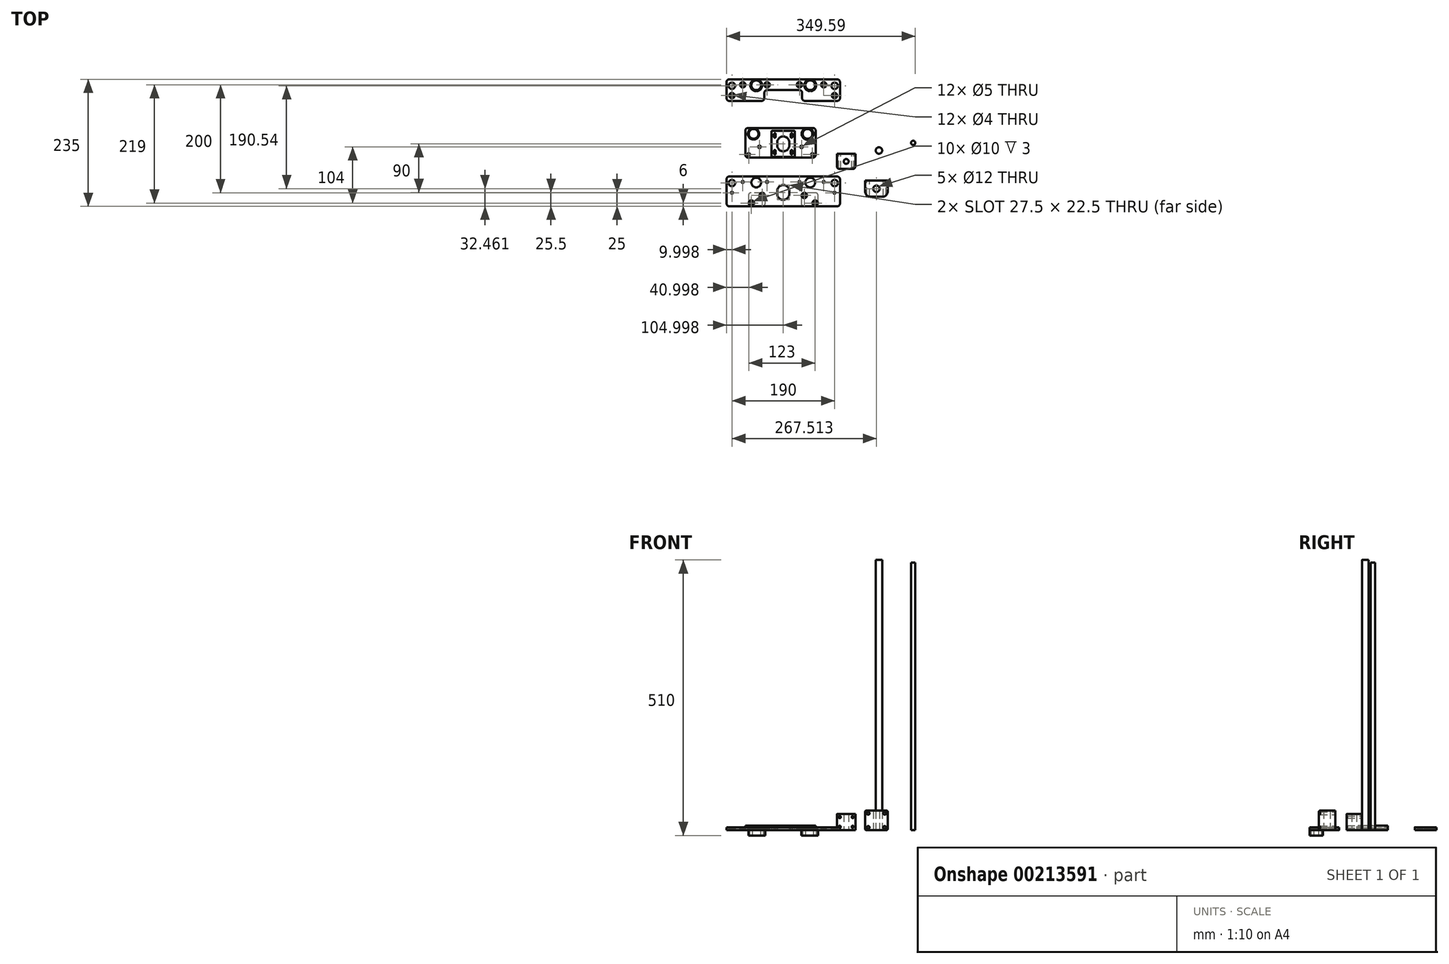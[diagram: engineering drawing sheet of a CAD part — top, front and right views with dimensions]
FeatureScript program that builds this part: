
annotation { "Feature Type Name" : "Feature", "Feature Type Description" : "" }
export const myFeature = defineFeature(function(context is Context, id is Id, definition is map)
    precondition{}
    {
        {
            var Q0;
            Q0=qCreatedBy(makeId("Top.planeOp"),FACE);
            var sketch = newSketch(context, id + "F0", { "sketchPlane" : qUnion([Q0])});
            skCircle(sketch, "E0", {"center": v(45.06, 37.07) * mm, "radius": 6 * mm});
            skSolve(sketch);
        }
        {
            var Q0;
            Q0=makeQuery(id+"F0.imprint","IMPRINT",FACE,{"disambiguationData":[TD([[makeQuery(id+"F0.imprint","IMPRINT",EDGE,{"derivedFrom":sQuery(id+"F0.wireOp",EDGE,"E0")}),1.0]])]});
            extrude(context, id + "F1", {"entities" : qUnion([Q0]), "depth" : 500 * mm});
        }
        {
            var Q0;
            Q0=qCreatedBy(makeId("Top.planeOp"),FACE);
            var sketch = newSketch(context, id + "F2", { "sketchPlane" : qUnion([Q0])});
            skLineSegment(sketch, "E1", {"start": v(-202.1, 78.9) * mm, "end": v(-202.1, 23.9) * mm});
            skLineSegment(sketch, "E2", {"start": v(-202.1, 23.9) * mm, "end": v(-72.1, 23.9) * mm});
            skLineSegment(sketch, "E3", {"start": v(-72.1, 23.9) * mm, "end": v(-72.1, 78.9) * mm});
            skLineSegment(sketch, "E4", {"start": v(-72.1, 78.9) * mm, "end": v(-202.1, 78.9) * mm});
            skCircle(sketch, "E5", {"center": v(-187.1, 67.9) * mm, "radius": 9 * mm});
            skCircle(sketch, "E6", {"center": v(-87.1, 67.9) * mm, "radius": 9 * mm});
            skLineSegment(sketch, "E7", {"start": v(-153.6, 25.4) * mm, "end": v(-153.6, 73.4) * mm});
            skLineSegment(sketch, "E8", {"start": v(-153.6, 73.4) * mm, "end": v(-110.6, 73.4) * mm});
            skLineSegment(sketch, "E9", {"start": v(-110.6, 73.4) * mm, "end": v(-110.6, 25.4) * mm});
            skLineSegment(sketch, "E10", {"start": v(-110.6, 25.4) * mm, "end": v(-153.6, 25.4) * mm});
            skLineSegment(sketch, "E11", {"start": v(-132.1, 73.4) * mm, "end": v(-132.1, 25.4) * mm, "construction": true});
            skLineSegment(sketch, "E12", {"start": v(-132.1, 49.4) * mm, "end": v(-143.35, 49.4) * mm, "construction": true});
            skLineSegment(sketch, "E13", {"start": v(-132.1, 49.4) * mm, "end": v(-120.85, 49.4) * mm, "construction": true});
            skLineSegment(sketch, "E14", {"start": v(-143.35, 51.9) * mm, "end": v(-143.35, 46.9) * mm});
            skLineSegment(sketch, "E15", {"start": v(-120.85, 51.9) * mm, "end": v(-120.85, 46.9) * mm});
            skArc(sketch, "E16", {"start": v(-120.85, 51.9) * mm, "mid": v(-132.1, 63.15) * mm, "end": v(-143.35, 51.9) * mm});
            skArc(sketch, "E17", {"start": v(-143.35, 46.9) * mm, "mid": v(-132.1, 35.65) * mm, "end": v(-120.85, 46.9) * mm});
            skLineSegment(sketch, "E18", {"start": v(-149.15, 36.4) * mm, "end": v(-149.15, 31.4) * mm});
            skLineSegment(sketch, "E19", {"start": v(-146.05, 36.4) * mm, "end": v(-146.05, 31.4) * mm});
            skArc(sketch, "E20", {"start": v(-146.05, 36.4) * mm, "mid": v(-147.6, 37.95) * mm, "end": v(-149.15, 36.4) * mm});
            skArc(sketch, "E21", {"start": v(-149.15, 31.4) * mm, "mid": v(-147.6, 29.85) * mm, "end": v(-146.05, 31.4) * mm});
            skLineSegment(sketch, "E22", {"start": v(-149.15, 33.9) * mm, "end": v(-146.05, 33.9) * mm, "construction": true});
            skLineSegment(sketch, "E23", {"start": v(-118.15, 36.4) * mm, "end": v(-118.15, 31.4) * mm});
            skLineSegment(sketch, "E24", {"start": v(-115.05, 36.4) * mm, "end": v(-115.05, 31.4) * mm});
            skArc(sketch, "E25", {"start": v(-115.05, 36.4) * mm, "mid": v(-116.6, 37.95) * mm, "end": v(-118.15, 36.4) * mm});
            skArc(sketch, "E26", {"start": v(-118.15, 31.4) * mm, "mid": v(-116.6, 29.85) * mm, "end": v(-115.05, 31.4) * mm});
            skLineSegment(sketch, "E27", {"start": v(-118.15, 33.9) * mm, "end": v(-115.05, 33.9) * mm, "construction": true});
            skLineSegment(sketch, "E28", {"start": v(-149.15, 67.4) * mm, "end": v(-149.15, 62.4) * mm});
            skLineSegment(sketch, "E29", {"start": v(-146.05, 67.4) * mm, "end": v(-146.05, 62.4) * mm});
            skArc(sketch, "E30", {"start": v(-146.05, 67.4) * mm, "mid": v(-147.6, 68.95) * mm, "end": v(-149.15, 67.4) * mm});
            skArc(sketch, "E31", {"start": v(-149.15, 62.4) * mm, "mid": v(-147.6, 60.85) * mm, "end": v(-146.05, 62.4) * mm});
            skLineSegment(sketch, "E32", {"start": v(-149.15, 64.9) * mm, "end": v(-146.05, 64.9) * mm, "construction": true});
            skLineSegment(sketch, "E33", {"start": v(-118.15, 67.4) * mm, "end": v(-118.15, 62.4) * mm});
            skLineSegment(sketch, "E34", {"start": v(-115.05, 67.4) * mm, "end": v(-115.05, 62.4) * mm});
            skArc(sketch, "E35", {"start": v(-115.05, 67.4) * mm, "mid": v(-116.6, 68.95) * mm, "end": v(-118.15, 67.4) * mm});
            skArc(sketch, "E36", {"start": v(-118.15, 62.4) * mm, "mid": v(-116.6, 60.85) * mm, "end": v(-115.05, 62.4) * mm});
            skLineSegment(sketch, "E37", {"start": v(-118.15, 64.9) * mm, "end": v(-115.05, 64.9) * mm, "construction": true});
            skCircle(sketch, "E38", {"center": v(-78.1, 29.9) * mm, "radius": 2.5 * mm});
            skCircle(sketch, "E39", {"center": v(-196.1, 29.9) * mm, "radius": 2.5 * mm});
            skCircle(sketch, "E40", {"center": v(-176.1, 43.9) * mm, "radius": 2.5 * mm});
            skCircle(sketch, "E41", {"center": v(-98.1, 43.9) * mm, "radius": 2.5 * mm});
            skSolve(sketch);
        }
        {
            var Q0;
            Q0=makeQuery(id+"F2.imprint","IMPRINT",FACE,{"disambiguationData":[TD([[makeQuery(id+"F2.imprint","IMPRINT",EDGE,{"derivedFrom":sQuery(id+"F2.wireOp",EDGE,"E1")}),1.0]])]});
            extrude(context, id + "F3", {"entities" : qUnion([Q0]), "depth" : 8 * mm});
        }
        {
            var Q0;
            Q0=makeQuery(id+"F2.imprint","IMPRINT",FACE,{"disambiguationData":[TD([[makeQuery(id+"F2.imprint","IMPRINT",EDGE,{"derivedFrom":sQuery(id+"F2.wireOp",EDGE,"E7")}),-1.0]])]});
            extrude(context, id + "F4", {"entities" : qUnion([Q0]), "operationType" : NewBodyOperationType.ADD, "depth" : 4 * mm});
        }
        {
            var Q0;
            Q0=makeQuery(id+"F3.opExtrude","SWEPT_EDGE",EDGE,{"disambiguationData":[OSD([sQuery(id+"F2.wireOp",EDGE,"E7"),sQuery(id+"F2.wireOp",EDGE,"E8")])]});
            var Q1;
            Q1=makeQuery(id+"F3.opExtrude","SWEPT_EDGE",EDGE,{"disambiguationData":[OSD([sQuery(id+"F2.wireOp",EDGE,"E8"),sQuery(id+"F2.wireOp",EDGE,"E9")])]});
            var Q2;
            Q2=makeQuery(id+"F3.opExtrude","SWEPT_EDGE",EDGE,{"disambiguationData":[OSD([sQuery(id+"F2.wireOp",EDGE,"E9"),sQuery(id+"F2.wireOp",EDGE,"E10")])]});
            var Q3;
            Q3=makeQuery(id+"F3.opExtrude","SWEPT_EDGE",EDGE,{"disambiguationData":[OSD([sQuery(id+"F2.wireOp",EDGE,"E7"),sQuery(id+"F2.wireOp",EDGE,"E10")])]});
            fillet(context, id + "F5", {"entities" : qUnion([Q0, Q1, Q2, Q3]), "radius" : 1 * mm, "tangentPropagation" : true, "allowEdgeOverflow" : false});
        }
        {
            var Q0;
            Q0=makeQuery(id+"F3.opExtrude","CAP_FACE",FACE,{"disambiguationData":[OSD([sQuery(id+"F2.wireOp",EDGE,"E1"),sQuery(id+"F2.wireOp",EDGE,"E2"),sQuery(id+"F2.wireOp",EDGE,"E3"),sQuery(id+"F2.wireOp",EDGE,"E4"),sQuery(id+"F2.wireOp",EDGE,"E5"),sQuery(id+"F2.wireOp",EDGE,"E6"),sQuery(id+"F2.wireOp",EDGE,"E7"),sQuery(id+"F2.wireOp",EDGE,"E8"),sQuery(id+"F2.wireOp",EDGE,"E9"),sQuery(id+"F2.wireOp",EDGE,"E10")])],"isStart":false});
            var sketch = newSketch(context, id + "F6", { "sketchPlane" : qUnion([Q0])});
            skCircle(sketch, "E42", {"center": v(-187.1, 67.9) * mm, "radius": 10.5 * mm});
            skLineSegment(sketch, "E43", {"start": v(-194.1, 75.73) * mm, "end": v(-194.1, 78.9) * mm});
            skLineSegment(sketch, "E44", {"start": v(-180.1, 75.73) * mm, "end": v(-180.1, 78.9) * mm});
            skCircle(sketch, "E45", {"center": v(-87.1, 67.9) * mm, "radius": 11 * mm});
            skLineSegment(sketch, "E46", {"start": v(-94.1, 76.39) * mm, "end": v(-94.1, 78.9) * mm});
            skLineSegment(sketch, "E47", {"start": v(-80.1, 76.39) * mm, "end": v(-80.1, 78.9) * mm});
            skSolve(sketch);
        }
        {
            var Q0;
            Q0=makeQuery(id+"F6.imprint","IMPRINT",FACE,{"disambiguationData":[TD([[makeQuery(id+"F6.imprint","IMPRINT",EDGE,{"derivedFrom":sQuery(id+"F6.wireOp",EDGE,"GBhv8pRL-lCPt-Fi0s-pCJl-KyG8ppzGTcWA")}),1.0]])]});
            var Q1;
            Q1=makeQuery(id+"F6.imprint","IMPRINT",FACE,{"disambiguationData":[TD([[makeQuery(id+"F6.imprint","IMPRINT",EDGE,{"derivedFrom":sQuery(id+"F6.wireOp",EDGE,"E42")}),1.0]])]});
            var Q2;
            {var subQ0=sQuery(id+"F6.wireOp",EDGE,"E43");Q2=makeQuery(id+"F6.imprint","IMPRINT",FACE,{"disambiguationData":[TD([[makeQuery(id+"F6.imprint","IMPRINT",EDGE,{"derivedFrom":subQ0}),-1.0]])]});}
            var Q3;
            {var subQ0=sQuery(id+"F6.wireOp",EDGE,"E44");Q3=makeQuery(id+"F6.imprint","IMPRINT",FACE,{"disambiguationData":[TD([[makeQuery(id+"F6.imprint","IMPRINT",EDGE,{"derivedFrom":subQ0}),1.0]])]});}
            var Q4;
            Q4=makeQuery(id+"F6.imprint","IMPRINT",FACE,{"disambiguationData":[TD([[makeQuery(id+"F6.imprint","IMPRINT",EDGE,{"derivedFrom":makeQuery(id+"F3.opExtrude","CAP_EDGE",EDGE,{"disambiguationData":[OSD([sQuery(id+"F2.wireOp",EDGE,"E6")])],"isStart":false})}),-1.0]])]});
            var Q5;
            {var subQ0=sQuery(id+"F6.wireOp",EDGE,"E46");Q5=makeQuery(id+"F6.imprint","IMPRINT",FACE,{"disambiguationData":[TD([[makeQuery(id+"F6.imprint","IMPRINT",EDGE,{"derivedFrom":subQ0}),-1.0]])]});}
            var Q6;
            {var subQ0=sQuery(id+"F6.wireOp",EDGE,"E47");Q6=makeQuery(id+"F6.imprint","IMPRINT",FACE,{"disambiguationData":[TD([[makeQuery(id+"F6.imprint","IMPRINT",EDGE,{"derivedFrom":subQ0}),1.0]])]});}
            extrude(context, id + "F7", {"entities" : qUnion([Q0, Q1, Q2, Q3, Q4, Q5, Q6]), "operationType" : NewBodyOperationType.REMOVE, "oppositeDirection" : true, "depth" : 5 * mm});
        }
        {
            var Q0;
            Q0=makeQuery(id+"F3.opExtrude","SWEPT_EDGE",EDGE,{"disambiguationData":[OSD([sQuery(id+"F2.wireOp",EDGE,"E1"),sQuery(id+"F2.wireOp",EDGE,"E4")])]});
            var Q1;
            Q1=makeQuery(id+"F3.opExtrude","SWEPT_EDGE",EDGE,{"disambiguationData":[OSD([sQuery(id+"F2.wireOp",EDGE,"E1"),sQuery(id+"F2.wireOp",EDGE,"E2")])]});
            var Q2;
            Q2=makeQuery(id+"F3.opExtrude","SWEPT_EDGE",EDGE,{"disambiguationData":[OSD([sQuery(id+"F2.wireOp",EDGE,"E2"),sQuery(id+"F2.wireOp",EDGE,"E3")])]});
            var Q3;
            Q3=makeQuery(id+"F3.opExtrude","SWEPT_EDGE",EDGE,{"disambiguationData":[OSD([sQuery(id+"F2.wireOp",EDGE,"E3"),sQuery(id+"F2.wireOp",EDGE,"E4")])]});
            fillet(context, id + "F8", {"entities" : qUnion([Q0, Q1, Q2, Q3]), "radius" : 5 * mm, "tangentPropagation" : true, "allowEdgeOverflow" : false});
        }
        {
            var Q0;
            Q0=qCreatedBy(makeId("Top.planeOp"),FACE);
            var sketch = newSketch(context, id + "F9", { "sketchPlane" : qUnion([Q0])});
            skLineSegment(sketch, "E48", {"start": v(-237.1, -11.1) * mm, "end": v(-237.1, -66.1) * mm});
            skLineSegment(sketch, "E49", {"start": v(-237.1, -66.1) * mm, "end": v(-27.1, -66.1) * mm});
            skLineSegment(sketch, "E50", {"start": v(-27.1, -66.1) * mm, "end": v(-27.1, -11.1) * mm});
            skLineSegment(sketch, "E51", {"start": v(-27.1, -11.1) * mm, "end": v(-237.1, -11.1) * mm});
            skLineSegment(sketch, "E52", {"start": v(-132.1, -40.6) * mm, "end": v(-143.35, -40.6) * mm, "construction": true});
            skLineSegment(sketch, "E53", {"start": v(-132.1, -40.6) * mm, "end": v(-120.85, -40.6) * mm, "construction": true});
            skLineSegment(sketch, "E54", {"start": v(-143.35, -38.1) * mm, "end": v(-143.35, -43.1) * mm});
            skLineSegment(sketch, "E55", {"start": v(-120.85, -38.1) * mm, "end": v(-120.85, -43.1) * mm});
            skArc(sketch, "E56", {"start": v(-120.85, -38.1) * mm, "mid": v(-132.1, -26.85) * mm, "end": v(-143.35, -38.1) * mm});
            skArc(sketch, "E57", {"start": v(-143.35, -43.1) * mm, "mid": v(-132.1, -54.35) * mm, "end": v(-120.85, -43.1) * mm});
            skCircle(sketch, "E58", {"center": v(-73.1, -60.1) * mm, "radius": 2.5 * mm});
            skCircle(sketch, "E59", {"center": v(-191.1, -60.1) * mm, "radius": 2.5 * mm});
            skCircle(sketch, "E60", {"center": v(-171.1, -46.1) * mm, "radius": 2.5 * mm});
            skCircle(sketch, "E61", {"center": v(-93.1, -46.1) * mm, "radius": 2.5 * mm});
            skCircle(sketch, "E62", {"center": v(-227.1, -23.1) * mm, "radius": 6 * mm});
            skCircle(sketch, "E63", {"center": v(-37.1, -23.1) * mm, "radius": 6 * mm});
            skCircle(sketch, "E64", {"center": v(-207.1, -21.1) * mm, "radius": 2 * mm});
            skCircle(sketch, "E65", {"center": v(-57.1, -21.1) * mm, "radius": 2 * mm});
            skCircle(sketch, "E66", {"center": v(-102.1, -21.1) * mm, "radius": 2 * mm});
            skCircle(sketch, "E67", {"center": v(-162.1, -21.1) * mm, "radius": 2 * mm});
            skCircle(sketch, "E68", {"center": v(-227.1, -41.1) * mm, "radius": 2 * mm});
            skCircle(sketch, "E69", {"center": v(-37.1, -41.1) * mm, "radius": 2 * mm});
            skCircle(sketch, "E70", {"center": v(-82.1, -22.1) * mm, "radius": 9 * mm});
            skCircle(sketch, "E71", {"center": v(-182.1, -22.1) * mm, "radius": 9 * mm});
            skSolve(sketch);
        }
        {
            var Q0;
            Q0=makeQuery(id+"F9.imprint","IMPRINT",FACE,{"disambiguationData":[TD([[makeQuery(id+"F9.imprint","IMPRINT",EDGE,{"derivedFrom":sQuery(id+"F9.wireOp",EDGE,"E48")}),1.0]])]});
            extrude(context, id + "F10", {"entities" : qUnion([Q0]), "depth" : 5 * mm});
        }
        {
            var Q0;
            Q0=makeQuery(id+"F10.opExtrude","CAP_FACE",FACE,{"disambiguationData":[OSD([sQuery(id+"F9.wireOp",EDGE,"E48"),sQuery(id+"F9.wireOp",EDGE,"E49"),sQuery(id+"F9.wireOp",EDGE,"E50"),sQuery(id+"F9.wireOp",EDGE,"E51"),sQuery(id+"F9.wireOp",EDGE,"E54"),sQuery(id+"F9.wireOp",EDGE,"E55"),sQuery(id+"F9.wireOp",EDGE,"E56"),sQuery(id+"F9.wireOp",EDGE,"E57"),sQuery(id+"F9.wireOp",EDGE,"E58"),sQuery(id+"F9.wireOp",EDGE,"E59"),sQuery(id+"F9.wireOp",EDGE,"E60"),sQuery(id+"F9.wireOp",EDGE,"E61"),sQuery(id+"F9.wireOp",EDGE,"E62"),sQuery(id+"F9.wireOp",EDGE,"E63"),sQuery(id+"F9.wireOp",EDGE,"E64"),sQuery(id+"F9.wireOp",EDGE,"E65"),sQuery(id+"F9.wireOp",EDGE,"E66"),sQuery(id+"F9.wireOp",EDGE,"E67"),sQuery(id+"F9.wireOp",EDGE,"E68"),sQuery(id+"F9.wireOp",EDGE,"E69")])],"isStart":false});
            var sketch = newSketch(context, id + "F11", { "sketchPlane" : qUnion([Q0])});
            skCircle(sketch, "E72", {"center": v(-191.1, -60.1) * mm, "radius": 5 * mm});
            skCircle(sketch, "E73", {"center": v(-171.1, -46.1) * mm, "radius": 5 * mm});
            skCircle(sketch, "E74", {"center": v(-93.1, -46.1) * mm, "radius": 5 * mm});
            skCircle(sketch, "E75", {"center": v(-73.1, -60.1) * mm, "radius": 5 * mm});
            skSolve(sketch);
        }
        {
            var Q0;
            Q0=makeQuery(id+"F11.imprint","IMPRINT",FACE,{"disambiguationData":[TD([[makeQuery(id+"F11.imprint","IMPRINT",EDGE,{"derivedFrom":sQuery(id+"F11.wireOp",EDGE,"E72")}),1.0]])]});
            var Q1;
            Q1=makeQuery(id+"F11.imprint","IMPRINT",FACE,{"disambiguationData":[TD([[makeQuery(id+"F11.imprint","IMPRINT",EDGE,{"derivedFrom":sQuery(id+"F11.wireOp",EDGE,"E73")}),1.0]])]});
            var Q2;
            Q2=makeQuery(id+"F11.imprint","IMPRINT",FACE,{"disambiguationData":[TD([[makeQuery(id+"F11.imprint","IMPRINT",EDGE,{"derivedFrom":sQuery(id+"F11.wireOp",EDGE,"E74")}),1.0]])]});
            var Q3;
            Q3=makeQuery(id+"F11.imprint","IMPRINT",FACE,{"disambiguationData":[TD([[makeQuery(id+"F11.imprint","IMPRINT",EDGE,{"derivedFrom":sQuery(id+"F11.wireOp",EDGE,"E75")}),1.0]])]});
            extrude(context, id + "F12", {"entities" : qUnion([Q0, Q1, Q2, Q3]), "operationType" : NewBodyOperationType.REMOVE, "oppositeDirection" : true, "depth" : 3 * mm});
        }
        {
            var Q0;
            Q0=makeQuery(id+"F10.opExtrude","SWEPT_EDGE",EDGE,{"disambiguationData":[OSD([sQuery(id+"F9.wireOp",EDGE,"E48"),sQuery(id+"F9.wireOp",EDGE,"E51")])]});
            var Q1;
            Q1=makeQuery(id+"F10.opExtrude","SWEPT_EDGE",EDGE,{"disambiguationData":[OSD([sQuery(id+"F9.wireOp",EDGE,"E48"),sQuery(id+"F9.wireOp",EDGE,"E49")])]});
            var Q2;
            Q2=makeQuery(id+"F10.opExtrude","SWEPT_EDGE",EDGE,{"disambiguationData":[OSD([sQuery(id+"F9.wireOp",EDGE,"E49"),sQuery(id+"F9.wireOp",EDGE,"E50")])]});
            var Q3;
            Q3=makeQuery(id+"F10.opExtrude","SWEPT_EDGE",EDGE,{"disambiguationData":[OSD([sQuery(id+"F9.wireOp",EDGE,"E50"),sQuery(id+"F9.wireOp",EDGE,"E51")])]});
            fillet(context, id + "F13", {"entities" : qUnion([Q0, Q1, Q2, Q3]), "radius" : 5 * mm, "tangentPropagation" : true, "allowEdgeOverflow" : false});
        }
        {
            var Q0;
            Q0=makeQuery(id+"F10.opExtrude","CAP_FACE",FACE,{"disambiguationData":[OSD([sQuery(id+"F9.wireOp",EDGE,"E48"),sQuery(id+"F9.wireOp",EDGE,"E49"),sQuery(id+"F9.wireOp",EDGE,"E50"),sQuery(id+"F9.wireOp",EDGE,"E51"),sQuery(id+"F9.wireOp",EDGE,"E54"),sQuery(id+"F9.wireOp",EDGE,"E55"),sQuery(id+"F9.wireOp",EDGE,"E56"),sQuery(id+"F9.wireOp",EDGE,"E57"),sQuery(id+"F9.wireOp",EDGE,"E58"),sQuery(id+"F9.wireOp",EDGE,"E59"),sQuery(id+"F9.wireOp",EDGE,"E60"),sQuery(id+"F9.wireOp",EDGE,"E61"),sQuery(id+"F9.wireOp",EDGE,"E62"),sQuery(id+"F9.wireOp",EDGE,"E63"),sQuery(id+"F9.wireOp",EDGE,"E64"),sQuery(id+"F9.wireOp",EDGE,"E65"),sQuery(id+"F9.wireOp",EDGE,"E66"),sQuery(id+"F9.wireOp",EDGE,"E67"),sQuery(id+"F9.wireOp",EDGE,"E68"),sQuery(id+"F9.wireOp",EDGE,"E69")])],"isStart":true});
            var sketch = newSketch(context, id + "F14", { "sketchPlane" : qUnion([Q0])});
            skLineSegment(sketch, "E76", {"start": v(-67.6, 66.1) * mm, "end": v(-67.6, 41.1) * mm});
            skLineSegment(sketch, "E77", {"start": v(-67.6, 41.1) * mm, "end": v(-98.6, 41.1) * mm});
            skLineSegment(sketch, "E78", {"start": v(-98.6, 41.1) * mm, "end": v(-98.6, 66.1) * mm});
            skLineSegment(sketch, "E79", {"start": v(-98.6, 66.1) * mm, "end": v(-67.6, 66.1) * mm});
            skLineSegment(sketch, "E80", {"start": v(-165.6, 66.1) * mm, "end": v(-165.6, 41.1) * mm});
            skLineSegment(sketch, "E81", {"start": v(-165.6, 41.1) * mm, "end": v(-196.6, 41.1) * mm});
            skLineSegment(sketch, "E82", {"start": v(-196.6, 41.1) * mm, "end": v(-196.6, 66.1) * mm});
            skLineSegment(sketch, "E83", {"start": v(-196.6, 66.1) * mm, "end": v(-165.6, 66.1) * mm});
            skSolve(sketch);
        }
        {
            var Q0;
            Q0=makeQuery(id+"F14.imprint","IMPRINT",FACE,{"disambiguationData":[TD([[makeQuery(id+"F14.imprint","IMPRINT",EDGE,{"derivedFrom":sQuery(id+"F14.wireOp",EDGE,"E76")}),-1.0]])]});
            var Q1;
            Q1=makeQuery(id+"F14.imprint","IMPRINT",FACE,{"disambiguationData":[TD([[makeQuery(id+"F14.imprint","IMPRINT",EDGE,{"derivedFrom":sQuery(id+"F14.wireOp",EDGE,"E80")}),-1.0]])]});
            extrude(context, id + "F15", {"entities" : qUnion([Q0, Q1]), "depth" : 10 * mm});
        }
        {
            var Q0;
            Q0=makeQuery(id+"F15.opExtrude","SWEPT_EDGE",EDGE,{"disambiguationData":[OSD([sQuery(id+"F9.wireOp",EDGE,"E49"),sQuery(id+"F14.wireOp",EDGE,"E78"),sQuery(id+"F14.wireOp",EDGE,"E79")])]});
            var Q1;
            Q1=makeQuery(id+"F15.opExtrude","SWEPT_EDGE",EDGE,{"disambiguationData":[OSD([sQuery(id+"F14.wireOp",EDGE,"E77"),sQuery(id+"F14.wireOp",EDGE,"E78")])]});
            var Q2;
            Q2=makeQuery(id+"F15.opExtrude","SWEPT_EDGE",EDGE,{"disambiguationData":[OSD([sQuery(id+"F9.wireOp",EDGE,"E49"),sQuery(id+"F14.wireOp",EDGE,"E76"),sQuery(id+"F14.wireOp",EDGE,"E79")])]});
            var Q3;
            Q3=makeQuery(id+"F15.opExtrude","SWEPT_EDGE",EDGE,{"disambiguationData":[OSD([sQuery(id+"F14.wireOp",EDGE,"E76"),sQuery(id+"F14.wireOp",EDGE,"E77")])]});
            var Q4;
            Q4=makeQuery(id+"F15.opExtrude","SWEPT_EDGE",EDGE,{"disambiguationData":[OSD([sQuery(id+"F14.wireOp",EDGE,"E80"),sQuery(id+"F14.wireOp",EDGE,"E81")])]});
            var Q5;
            Q5=makeQuery(id+"F15.opExtrude","SWEPT_EDGE",EDGE,{"disambiguationData":[OSD([sQuery(id+"F9.wireOp",EDGE,"E49"),sQuery(id+"F14.wireOp",EDGE,"E80"),sQuery(id+"F14.wireOp",EDGE,"E83")])]});
            var Q6;
            Q6=makeQuery(id+"F15.opExtrude","SWEPT_EDGE",EDGE,{"disambiguationData":[OSD([sQuery(id+"F9.wireOp",EDGE,"E49"),sQuery(id+"F14.wireOp",EDGE,"E82"),sQuery(id+"F14.wireOp",EDGE,"E83")])]});
            var Q7;
            Q7=makeQuery(id+"F15.opExtrude","SWEPT_EDGE",EDGE,{"disambiguationData":[OSD([sQuery(id+"F14.wireOp",EDGE,"E81"),sQuery(id+"F14.wireOp",EDGE,"E82")])]});
            fillet(context, id + "F16", {"entities" : qUnion([Q0, Q1, Q2, Q3, Q4, Q5, Q6, Q7]), "radius" : 5 * mm, "tangentPropagation" : true, "allowEdgeOverflow" : false});
        }
        {
            var Q0;
            Q0=qCreatedBy(makeId("Top.planeOp"),FACE);
            var sketch = newSketch(context, id + "F17", { "sketchPlane" : qUnion([Q0])});
            skLineSegment(sketch, "E84", {"start": v(-237.1, 168.9) * mm, "end": v(-237.1, 128.9) * mm});
            skLineSegment(sketch, "E85", {"start": v(-237.1, 128.9) * mm, "end": v(-27.1, 128.9) * mm});
            skLineSegment(sketch, "E86", {"start": v(-27.1, 128.9) * mm, "end": v(-27.1, 168.9) * mm});
            skLineSegment(sketch, "E87", {"start": v(-27.1, 168.9) * mm, "end": v(-237.1, 168.9) * mm});
            skCircle(sketch, "E88", {"center": v(-227.1, 156.9) * mm, "radius": 6 * mm});
            skCircle(sketch, "E89", {"center": v(-37.1, 156.9) * mm, "radius": 6 * mm});
            skCircle(sketch, "E90", {"center": v(-207.1, 158.9) * mm, "radius": 2 * mm});
            skCircle(sketch, "E91", {"center": v(-57.1, 158.9) * mm, "radius": 2 * mm});
            skCircle(sketch, "E92", {"center": v(-102.1, 158.9) * mm, "radius": 2 * mm});
            skCircle(sketch, "E93", {"center": v(-162.1, 158.9) * mm, "radius": 2 * mm});
            skCircle(sketch, "E94", {"center": v(-227.1, 138.9) * mm, "radius": 2 * mm});
            skCircle(sketch, "E95", {"center": v(-37.1, 138.9) * mm, "radius": 2 * mm});
            skCircle(sketch, "E96", {"center": v(-82.1, 157.9) * mm, "radius": 9 * mm});
            skCircle(sketch, "E97", {"center": v(-182.1, 157.9) * mm, "radius": 9 * mm});
            skLineSegment(sketch, "E98", {"start": v(-167.1, 128.9) * mm, "end": v(-167.1, 148.9) * mm});
            skLineSegment(sketch, "E99", {"start": v(-167.1, 148.9) * mm, "end": v(-97.1, 148.9) * mm});
            skLineSegment(sketch, "E100", {"start": v(-97.1, 148.9) * mm, "end": v(-97.1, 128.9) * mm});
            skSolve(sketch);
        }
        {
            var Q0;
            Q0=makeQuery(id+"F17.imprint","IMPRINT",FACE,{"disambiguationData":[TD([[makeQuery(id+"F17.imprint","IMPRINT",EDGE,{"derivedFrom":sQuery(id+"F17.wireOp",EDGE,"E84")}),1.0]])]});
            extrude(context, id + "F18", {"entities" : qUnion([Q0]), "depth" : 5 * mm});
        }
        {
            var Q0;
            Q0=makeQuery(id+"F18.opExtrude","CAP_FACE",FACE,{"disambiguationData":[OSD([sQuery(id+"F17.wireOp",EDGE,"E84"),sQuery(id+"F17.wireOp",EDGE,"E85"),sQuery(id+"F17.wireOp",EDGE,"E86"),sQuery(id+"F17.wireOp",EDGE,"E87"),sQuery(id+"F17.wireOp",EDGE,"E88"),sQuery(id+"F17.wireOp",EDGE,"E89"),sQuery(id+"F17.wireOp",EDGE,"E90"),sQuery(id+"F17.wireOp",EDGE,"E91"),sQuery(id+"F17.wireOp",EDGE,"E92"),sQuery(id+"F17.wireOp",EDGE,"E93"),sQuery(id+"F17.wireOp",EDGE,"E94"),sQuery(id+"F17.wireOp",EDGE,"E95"),sQuery(id+"F17.wireOp",EDGE,"E96"),sQuery(id+"F17.wireOp",EDGE,"E97")])],"isStart":false});
            var sketch = newSketch(context, id + "F19", { "sketchPlane" : qUnion([Q0])});
            skCircle(sketch, "E101", {"center": v(-182.1, 157.9) * mm, "radius": 11 * mm});
            skCircle(sketch, "E102", {"center": v(-82.1, 157.9) * mm, "radius": 11 * mm});
            skCircle(sketch, "E103", {"center": v(-207.1, 158.9) * mm, "radius": 5 * mm});
            skCircle(sketch, "E104", {"center": v(-227.1, 138.9) * mm, "radius": 5 * mm});
            skCircle(sketch, "E105", {"center": v(-162.1, 158.9) * mm, "radius": 5 * mm});
            skCircle(sketch, "E106", {"center": v(-102.1, 158.9) * mm, "radius": 5 * mm});
            skCircle(sketch, "E107", {"center": v(-57.1, 158.9) * mm, "radius": 5 * mm});
            skCircle(sketch, "E108", {"center": v(-37.1, 138.9) * mm, "radius": 5 * mm});
            skLineSegment(sketch, "E109", {"start": v(-189.1, 166.39) * mm, "end": v(-189.1, 168.9) * mm});
            skLineSegment(sketch, "E110", {"start": v(-175.1, 166.39) * mm, "end": v(-175.1, 168.9) * mm});
            skLineSegment(sketch, "E111", {"start": v(-89.1, 166.39) * mm, "end": v(-89.1, 168.9) * mm});
            skLineSegment(sketch, "E112", {"start": v(-75.1, 166.39) * mm, "end": v(-75.1, 168.9) * mm});
            skSolve(sketch);
        }
        {
            var Q0;
            Q0=makeQuery(id+"F19.imprint","IMPRINT",FACE,{"disambiguationData":[TD([[makeQuery(id+"F19.imprint","IMPRINT",EDGE,{"derivedFrom":sQuery(id+"F19.wireOp",EDGE,"E102")}),1.0]])]});
            var Q1;
            Q1=makeQuery(id+"F19.imprint","IMPRINT",FACE,{"disambiguationData":[TD([[makeQuery(id+"F19.imprint","IMPRINT",EDGE,{"derivedFrom":sQuery(id+"F19.wireOp",EDGE,"E106")}),1.0]])]});
            var Q2;
            Q2=makeQuery(id+"F19.imprint","IMPRINT",FACE,{"disambiguationData":[TD([[makeQuery(id+"F19.imprint","IMPRINT",EDGE,{"derivedFrom":sQuery(id+"F19.wireOp",EDGE,"E107")}),1.0]])]});
            var Q3;
            Q3=makeQuery(id+"F19.imprint","IMPRINT",FACE,{"disambiguationData":[TD([[makeQuery(id+"F19.imprint","IMPRINT",EDGE,{"derivedFrom":sQuery(id+"F19.wireOp",EDGE,"E108")}),1.0]])]});
            var Q4;
            Q4=makeQuery(id+"F19.imprint","IMPRINT",FACE,{"disambiguationData":[TD([[makeQuery(id+"F19.imprint","IMPRINT",EDGE,{"derivedFrom":sQuery(id+"F19.wireOp",EDGE,"E105")}),1.0]])]});
            var Q5;
            Q5=makeQuery(id+"F19.imprint","IMPRINT",FACE,{"disambiguationData":[TD([[makeQuery(id+"F19.imprint","IMPRINT",EDGE,{"derivedFrom":sQuery(id+"F19.wireOp",EDGE,"E101")}),1.0]])]});
            var Q6;
            Q6=makeQuery(id+"F19.imprint","IMPRINT",FACE,{"disambiguationData":[TD([[makeQuery(id+"F19.imprint","IMPRINT",EDGE,{"derivedFrom":sQuery(id+"F19.wireOp",EDGE,"E103")}),1.0]])]});
            var Q7;
            Q7=makeQuery(id+"F19.imprint","IMPRINT",FACE,{"disambiguationData":[TD([[makeQuery(id+"F19.imprint","IMPRINT",EDGE,{"derivedFrom":sQuery(id+"F19.wireOp",EDGE,"E104")}),1.0]])]});
            var Q8;
            {var subQ0=sQuery(id+"F19.wireOp",EDGE,"E109");Q8=makeQuery(id+"F19.imprint","IMPRINT",FACE,{"disambiguationData":[TD([[makeQuery(id+"F19.imprint","IMPRINT",EDGE,{"derivedFrom":subQ0}),-1.0]])]});}
            var Q9;
            {var subQ0=sQuery(id+"F19.wireOp",EDGE,"E110");Q9=makeQuery(id+"F19.imprint","IMPRINT",FACE,{"disambiguationData":[TD([[makeQuery(id+"F19.imprint","IMPRINT",EDGE,{"derivedFrom":subQ0}),1.0]])]});}
            var Q10;
            {var subQ0=sQuery(id+"F19.wireOp",EDGE,"E111");Q10=makeQuery(id+"F19.imprint","IMPRINT",FACE,{"disambiguationData":[TD([[makeQuery(id+"F19.imprint","IMPRINT",EDGE,{"derivedFrom":subQ0}),-1.0]])]});}
            var Q11;
            {var subQ0=sQuery(id+"F19.wireOp",EDGE,"E112");Q11=makeQuery(id+"F19.imprint","IMPRINT",FACE,{"disambiguationData":[TD([[makeQuery(id+"F19.imprint","IMPRINT",EDGE,{"derivedFrom":subQ0}),1.0]])]});}
            extrude(context, id + "F20", {"entities" : qUnion([Q0, Q1, Q2, Q3, Q4, Q5, Q6, Q7, Q8, Q9, Q10, Q11]), "operationType" : NewBodyOperationType.REMOVE, "oppositeDirection" : true, "depth" : 3 * mm});
        }
        {
            var Q0;
            Q0=makeQuery(id+"F18.opExtrude","SWEPT_EDGE",EDGE,{"disambiguationData":[OSD([sQuery(id+"F17.wireOp",EDGE,"E84"),sQuery(id+"F17.wireOp",EDGE,"E85")])]});
            var Q1;
            Q1=makeQuery(id+"F18.opExtrude","SWEPT_EDGE",EDGE,{"disambiguationData":[OSD([sQuery(id+"F17.wireOp",EDGE,"E84"),sQuery(id+"F17.wireOp",EDGE,"E87")])]});
            var Q2;
            Q2=makeQuery(id+"F18.opExtrude","SWEPT_EDGE",EDGE,{"disambiguationData":[OSD([sQuery(id+"F17.wireOp",EDGE,"E85"),sQuery(id+"F17.wireOp",EDGE,"E98")])]});
            var Q3;
            Q3=makeQuery(id+"F18.opExtrude","SWEPT_EDGE",EDGE,{"disambiguationData":[OSD([sQuery(id+"F17.wireOp",EDGE,"E98"),sQuery(id+"F17.wireOp",EDGE,"E99")])]});
            var Q4;
            Q4=makeQuery(id+"F18.opExtrude","SWEPT_EDGE",EDGE,{"disambiguationData":[OSD([sQuery(id+"F17.wireOp",EDGE,"E99"),sQuery(id+"F17.wireOp",EDGE,"E100")])]});
            var Q5;
            Q5=makeQuery(id+"F18.opExtrude","SWEPT_EDGE",EDGE,{"disambiguationData":[OSD([sQuery(id+"F17.wireOp",EDGE,"E85"),sQuery(id+"F17.wireOp",EDGE,"E100")])]});
            var Q6;
            Q6=makeQuery(id+"F18.opExtrude","SWEPT_EDGE",EDGE,{"disambiguationData":[OSD([sQuery(id+"F17.wireOp",EDGE,"E85"),sQuery(id+"F17.wireOp",EDGE,"E86")])]});
            var Q7;
            Q7=makeQuery(id+"F18.opExtrude","SWEPT_EDGE",EDGE,{"disambiguationData":[OSD([sQuery(id+"F17.wireOp",EDGE,"E86"),sQuery(id+"F17.wireOp",EDGE,"E87")])]});
            fillet(context, id + "F21", {"entities" : qUnion([Q0, Q1, Q2, Q3, Q4, Q5, Q6, Q7]), "radius" : 5 * mm, "tangentPropagation" : true, "allowEdgeOverflow" : false});
        }
        {
            var Q0;
            Q0=qCreatedBy(makeId("Top.planeOp"),FACE);
            var sketch = newSketch(context, id + "F22", { "sketchPlane" : qUnion([Q0])});
            skLineSegment(sketch, "E113", {"start": v(19.41, -18.64) * mm, "end": v(19.41, -48.64) * mm});
            skLineSegment(sketch, "E114", {"start": v(19.41, -48.64) * mm, "end": v(61.41, -48.64) * mm});
            skLineSegment(sketch, "E115", {"start": v(61.41, -48.64) * mm, "end": v(61.41, -18.64) * mm});
            skLineSegment(sketch, "E116", {"start": v(61.41, -18.64) * mm, "end": v(19.41, -18.64) * mm});
            skCircle(sketch, "E117", {"center": v(40.41, -33.64) * mm, "radius": 6 * mm});
            skSolve(sketch);
        }
        {
            var Q0;
            Q0=makeQuery(id+"F22.imprint","IMPRINT",FACE,{"disambiguationData":[TD([[makeQuery(id+"F22.imprint","IMPRINT",EDGE,{"derivedFrom":sQuery(id+"F22.wireOp",EDGE,"E113")}),1.0]])]});
            extrude(context, id + "F23", {"entities" : qUnion([Q0]), "depth" : 36 * mm});
        }
        {
            var Q0;
            Q0=makeQuery(id+"F23.opExtrude","SWEPT_EDGE",EDGE,{"disambiguationData":[OSD([sQuery(id+"F22.wireOp",EDGE,"E113"),sQuery(id+"F22.wireOp",EDGE,"E114")])]});
            var Q1;
            Q1=makeQuery(id+"F23.opExtrude","SWEPT_EDGE",EDGE,{"disambiguationData":[OSD([sQuery(id+"F22.wireOp",EDGE,"E114"),sQuery(id+"F22.wireOp",EDGE,"E115")])]});
            fillet(context, id + "F24", {"entities" : qUnion([Q0, Q1]), "radius" : 10 * mm, "tangentPropagation" : true, "allowEdgeOverflow" : false});
        }
        {
            var Q0;
            Q0=makeQuery(id+"F23.opExtrude","CAP_EDGE",EDGE,{"disambiguationData":[OSD([sQuery(id+"F22.wireOp",EDGE,"E114")])],"isStart":false});
            var Q1;
            Q1=makeQuery(id+"F23.opExtrude","CAP_EDGE",EDGE,{"disambiguationData":[OSD([sQuery(id+"F22.wireOp",EDGE,"E115")])],"isStart":true});
            fillet(context, id + "F25", {"entities" : qUnion([Q0, Q1]), "radius" : 2 * mm, "tangentPropagation" : true, "allowEdgeOverflow" : false});
        }
        {
            var Q0;
            Q0=makeQuery(id+"F23.opExtrude","SWEPT_FACE",FACE,{"disambiguationData":[OSD([sQuery(id+"F22.wireOp",EDGE,"E116")])]});
            var sketch = newSketch(context, id + "F26", { "sketchPlane" : qUnion([Q0])});
            skCircle(sketch, "E118", {"center": v(-55.66, 5) * mm, "radius": 2.5 * mm});
            skCircle(sketch, "E119", {"center": v(-55.66, 31) * mm, "radius": 2.5 * mm});
            skCircle(sketch, "E120", {"center": v(-25.16, 5) * mm, "radius": 2.5 * mm});
            skCircle(sketch, "E121", {"center": v(-25.16, 31) * mm, "radius": 2.5 * mm});
            skSolve(sketch);
        }
        {
            var Q0;
            Q0=makeQuery(id+"F26.imprint","IMPRINT",FACE,{"disambiguationData":[TD([[makeQuery(id+"F26.imprint","IMPRINT",EDGE,{"derivedFrom":sQuery(id+"F26.wireOp",EDGE,"E120")}),1.0]])]});
            var Q1;
            Q1=makeQuery(id+"F26.imprint","IMPRINT",FACE,{"disambiguationData":[TD([[makeQuery(id+"F26.imprint","IMPRINT",EDGE,{"derivedFrom":sQuery(id+"F26.wireOp",EDGE,"E121")}),1.0]])]});
            var Q2;
            Q2=makeQuery(id+"F26.imprint","IMPRINT",FACE,{"disambiguationData":[TD([[makeQuery(id+"F26.imprint","IMPRINT",EDGE,{"derivedFrom":sQuery(id+"F26.wireOp",EDGE,"E119")}),1.0]])]});
            var Q3;
            Q3=makeQuery(id+"F26.imprint","IMPRINT",FACE,{"disambiguationData":[TD([[makeQuery(id+"F26.imprint","IMPRINT",EDGE,{"derivedFrom":sQuery(id+"F26.wireOp",EDGE,"E118")}),1.0]])]});
            extrude(context, id + "F27", {"entities" : qUnion([Q0, Q1, Q2, Q3]), "operationType" : NewBodyOperationType.REMOVE, "oppositeDirection" : true, "depth" : 40 * mm});
        }
        {
            var Q0;
            Q0=qCreatedBy(makeId("Top.planeOp"),FACE);
            var sketch = newSketch(context, id + "F28", { "sketchPlane" : qUnion([Q0])});
            skCircle(sketch, "E122", {"center": v(108.49, 51.27) * mm, "radius": 4 * mm});
            skSolve(sketch);
        }
        {
            var Q0;
            Q0=makeQuery(id+"F28.imprint","IMPRINT",FACE,{"disambiguationData":[TD([[makeQuery(id+"F28.imprint","IMPRINT",EDGE,{"derivedFrom":sQuery(id+"F28.wireOp",EDGE,"E122")}),1.0]])]});
            extrude(context, id + "F29", {"entities" : qUnion([Q0]), "depth" : 495 * mm});
        }
        {
            var Q0;
            Q0=qCreatedBy(makeId("Top.planeOp"),FACE);
            var sketch = newSketch(context, id + "F30", { "sketchPlane" : qUnion([Q0])});
            skLineSegment(sketch, "E123", {"start": v(-32.54, 30.82) * mm, "end": v(-32.54, 2.82) * mm});
            skLineSegment(sketch, "E124", {"start": v(-32.54, 2.82) * mm, "end": v(1.46, 2.82) * mm});
            skLineSegment(sketch, "E125", {"start": v(1.46, 2.82) * mm, "end": v(1.46, 30.82) * mm});
            skLineSegment(sketch, "E126", {"start": v(1.46, 30.82) * mm, "end": v(-32.54, 30.82) * mm});
            skCircle(sketch, "E127", {"center": v(-15.54, 16.82) * mm, "radius": 4.5 * mm});
            skSolve(sketch);
        }
        {
            var Q0;
            Q0=makeQuery(id+"F30.imprint","IMPRINT",FACE,{"disambiguationData":[TD([[makeQuery(id+"F30.imprint","IMPRINT",EDGE,{"derivedFrom":sQuery(id+"F30.wireOp",EDGE,"E123")}),1.0]])]});
            extrude(context, id + "F31", {"entities" : qUnion([Q0]), "depth" : 30 * mm});
        }
        {
            var Q0;
            Q0=makeQuery(id+"F31.opExtrude","SWEPT_FACE",FACE,{"disambiguationData":[OSD([sQuery(id+"F30.wireOp",EDGE,"E126")])]});
            var sketch = newSketch(context, id + "F32", { "sketchPlane" : qUnion([Q0])});
            skCircle(sketch, "E128", {"center": v(27.54, 24) * mm, "radius": 2 * mm});
            skCircle(sketch, "E129", {"center": v(3.54, 24) * mm, "radius": 2 * mm});
            skCircle(sketch, "E130", {"center": v(27.54, 6) * mm, "radius": 2 * mm});
            skCircle(sketch, "E131", {"center": v(3.54, 6) * mm, "radius": 2 * mm});
            skSolve(sketch);
        }
        {
            var Q0;
            Q0=makeQuery(id+"F32.imprint","IMPRINT",FACE,{"disambiguationData":[TD([[makeQuery(id+"F32.imprint","IMPRINT",EDGE,{"derivedFrom":sQuery(id+"F32.wireOp",EDGE,"E128")}),1.0]])]});
            var Q1;
            Q1=makeQuery(id+"F32.imprint","IMPRINT",FACE,{"disambiguationData":[TD([[makeQuery(id+"F32.imprint","IMPRINT",EDGE,{"derivedFrom":sQuery(id+"F32.wireOp",EDGE,"E129")}),1.0]])]});
            var Q2;
            Q2=makeQuery(id+"F32.imprint","IMPRINT",FACE,{"disambiguationData":[TD([[makeQuery(id+"F32.imprint","IMPRINT",EDGE,{"derivedFrom":sQuery(id+"F32.wireOp",EDGE,"E131")}),1.0]])]});
            var Q3;
            Q3=makeQuery(id+"F32.imprint","IMPRINT",FACE,{"disambiguationData":[TD([[makeQuery(id+"F32.imprint","IMPRINT",EDGE,{"derivedFrom":sQuery(id+"F32.wireOp",EDGE,"E130")}),1.0]])]});
            extrude(context, id + "F33", {"entities" : qUnion([Q0, Q1, Q2, Q3]), "operationType" : NewBodyOperationType.REMOVE, "oppositeDirection" : true, "depth" : 35 * mm});
        }
        {
            var Q0;
            Q0=makeQuery(id+"F31.opExtrude","SWEPT_EDGE",EDGE,{"disambiguationData":[OSD([sQuery(id+"F30.wireOp",EDGE,"E123"),sQuery(id+"F30.wireOp",EDGE,"E124")])]});
            var Q1;
            Q1=makeQuery(id+"F31.opExtrude","SWEPT_EDGE",EDGE,{"disambiguationData":[OSD([sQuery(id+"F30.wireOp",EDGE,"E124"),sQuery(id+"F30.wireOp",EDGE,"E125")])]});
            fillet(context, id + "F34", {"entities" : qUnion([Q0, Q1]), "radius" : 5 * mm, "tangentPropagation" : true, "allowEdgeOverflow" : false});
        }
    });
